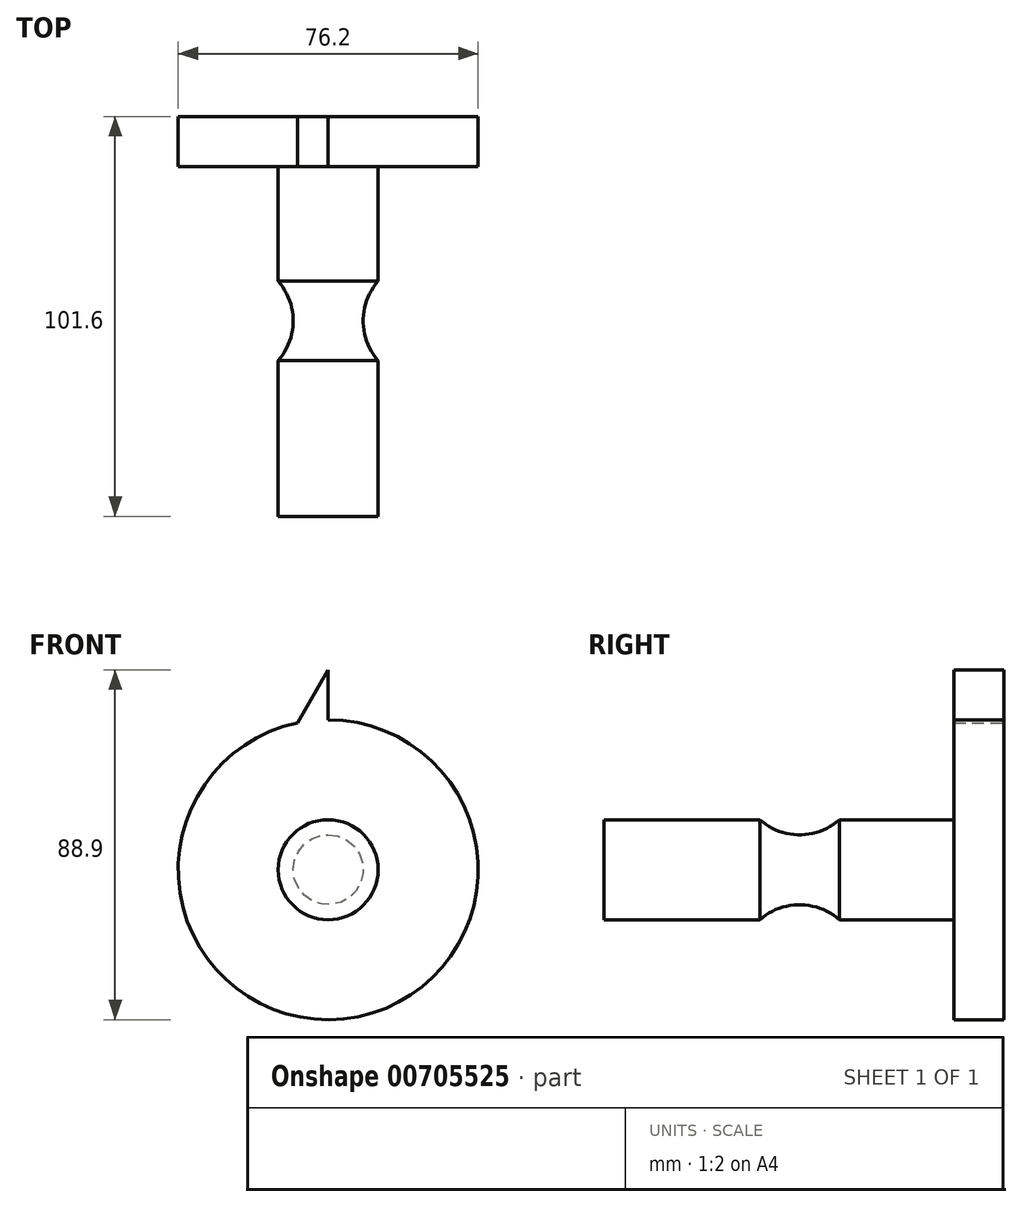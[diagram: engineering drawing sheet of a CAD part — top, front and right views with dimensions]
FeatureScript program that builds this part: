
annotation { "Feature Type Name" : "Feature", "Feature Type Description" : "" }
export const myFeature = defineFeature(function(context is Context, id is Id, definition is map)
    precondition{}
    {
        {
            var Q0;
            Q0=qCreatedBy(makeId("Front.planeOp"),FACE);
            var sketch = newSketch(context, id + "F0", { "sketchPlane" : qUnion([Q0])});
            skCircle(sketch, "E0", {"center": v(0, 0) * mm, "radius": 38.1 * mm});
            skSolve(sketch);
        }
        {
            var Q0;
            Q0=makeQuery(id+"F0.imprint","IMPRINT",FACE,{"disambiguationData":[TD([[makeQuery(id+"F0.imprint","IMPRINT",EDGE,{"derivedFrom":sQuery(id+"F0.wireOp",EDGE,"E0")}),1.0]])]});
            extrude(context, id + "F1", {"entities" : qUnion([Q0]), "depth" : 12.7 * mm, "offsetDistance" : 25.4 * mm});
        }
        {
            var Q0;
            Q0=qCreatedBy(makeId("Front.planeOp"),FACE);
            var sketch = newSketch(context, id + "F2", { "sketchPlane" : qUnion([Q0])});
            skLineSegment(sketch, "E1", {"start": v(-7.8, 37.3) * mm, "end": v(0, 38.1) * mm});
            skLineSegment(sketch, "E2", {"start": v(0, 38.1) * mm, "end": v(0, 50.8) * mm});
            skLineSegment(sketch, "E3", {"start": v(0, 50.8) * mm, "end": v(-7.8, 37.3) * mm});
            skLineSegment(sketch, "E4", {"start": v(0, 0) * mm, "end": v(0, 50.8) * mm, "construction": true});
            skSolve(sketch);
        }
        {
            var Q0;
            Q0=makeQuery(id+"F2.imprint","IMPRINT",FACE,{"disambiguationData":[TD([[makeQuery(id+"F2.imprint","IMPRINT",EDGE,{"derivedFrom":sQuery(id+"F2.wireOp",EDGE,"E1")}),1.0]])]});
            var Q1;
            Q1=makeQuery(id+"F1.opExtrude","CAP_FACE",FACE,{"disambiguationData":[OSD([sQuery(id+"F0.wireOp",EDGE,"E0")])],"isStart":false});
            extrude(context, id + "F3", {"entities" : qUnion([Q0]), "operationType" : NewBodyOperationType.ADD, "endBound" : BoundingType.UP_TO_SURFACE, "depth" : 12.7 * mm, "endBoundEntityFace" : qUnion([Q1]), "offsetDistance" : 25.4 * mm});
        }
        {
            var Q0;
            Q0=qCreatedBy(makeId("Front.planeOp"),FACE);
            var sketch = newSketch(context, id + "F4", { "sketchPlane" : qUnion([Q0])});
            skCircle(sketch, "E5", {"center": v(0, 0) * mm, "radius": 12.7 * mm});
            skSolve(sketch);
        }
        {
            var Q0;
            Q0 = qSketchRegion(id + "F4", true);
            extrude(context, id + "F5", {"entities" : qUnion([Q0]), "operationType" : NewBodyOperationType.ADD, "depth" : 101.6 * mm, "offsetDistance" : 25.4 * mm});
        }
        {
            var Q0;
            Q0=qCreatedBy(makeId("Right.planeOp"),FACE);
            var sketch = newSketch(context, id + "F6", { "sketchPlane" : qUnion([Q0])});
            skArc(sketch, "E6", {"start": v(-65.8, 17.78) * mm, "mid": v(-51.95, 8.89) * mm, "end": v(-38.1, 17.78) * mm});
            skLineSegment(sketch, "E7", {"start": v(-101.6, 17.78) * mm, "end": v(0, 17.78) * mm, "construction": true});
            skLineSegment(sketch, "E8", {"start": v(-38.1, 17.78) * mm, "end": v(-65.8, 17.78) * mm});
            skSolve(sketch);
        }
        {
            var Q0;
            Q0 = qSketchRegion(id + "F6", true);
            var Q1;
            Q1=makeQuery(id+"F5.opExtrude","SWEPT_FACE",FACE,{"disambiguationData":[OSD([sQuery(id+"F4.wireOp",EDGE,"E5")])]});
            revolve(context, id + "F7", {"operationType" : NewBodyOperationType.REMOVE, "surfaceOperationType" : NewSurfaceOperationType.NEW, "entities" : qUnion([Q0]), "axis" : qUnion([Q1]), "revolveType" : RevolveType.FULL, "oppositeDirection" : true});
        }
    });
